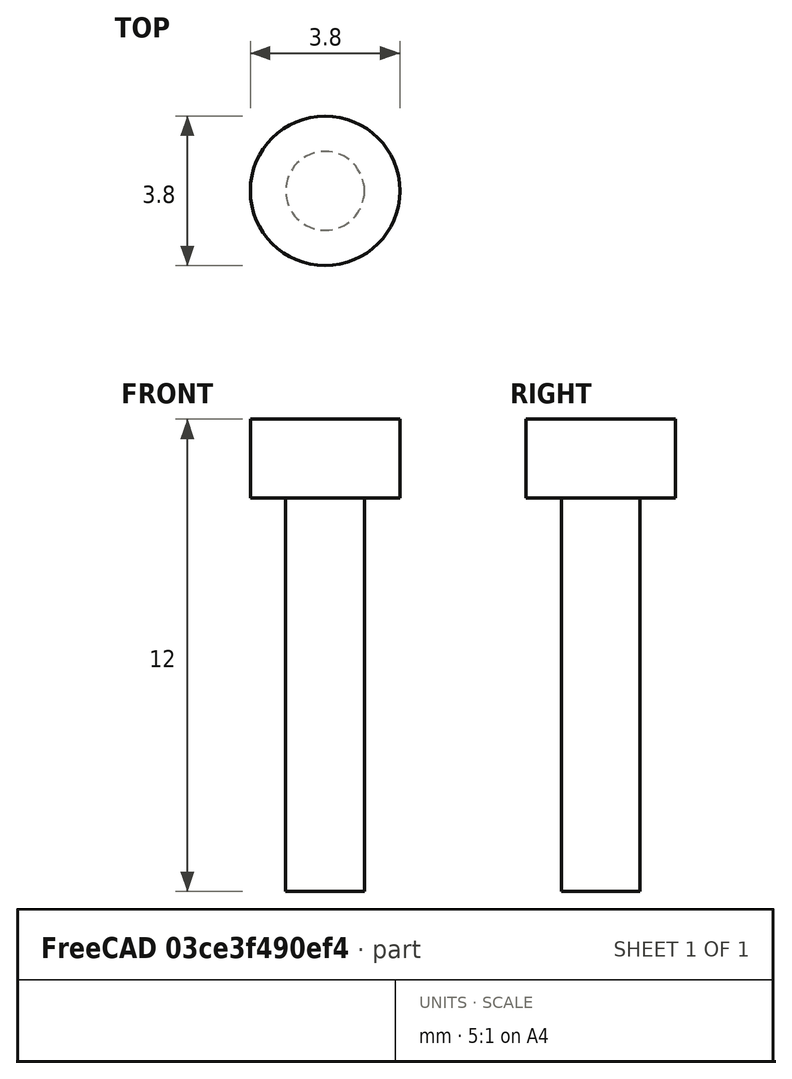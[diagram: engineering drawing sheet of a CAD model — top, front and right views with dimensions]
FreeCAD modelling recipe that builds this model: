
FCSTD DOCUMENT  (FreeCAD 0.18R14555 (Git shallow))
Label: m2-10
License: All rights reserved
LicenseURL: http://en.wikipedia.org/wiki/All_rights_reserved
objects: Sketcher::SketchObject×1, PartDesign::Revolution×1, PartDesign::Body×1
note: 4 computed .brp shape members not serialized (recipe doc carries the construction recipe); baked Part::Feature solids carry a one-line shape summary decoded from their .brp

FEATURE [Sketcher::SketchObject] Sketch
  MapMode = 5
  Placement = pos=(0,0,0) rot=(1,0,0;1.5708rad)
  Support = -> [XZ_Plane]
  sketch-geometry (6):
    g0: LineSegment StartX=0 StartY=0 StartZ=0 EndX=1 EndY=0 EndZ=0
    g1: LineSegment StartX=1 StartY=0 StartZ=0 EndX=1 EndY=10 EndZ=0
    g2: LineSegment StartX=1 StartY=10 StartZ=0 EndX=1.9 EndY=10 EndZ=0
    g3: LineSegment StartX=1.9 StartY=10 StartZ=0 EndX=1.9 EndY=12 EndZ=0
    g4: LineSegment StartX=1.9 StartY=12 StartZ=0 EndX=0 EndY=12 EndZ=0
    g5: LineSegment StartX=0 StartY=12 StartZ=0 EndX=0 EndY=0 EndZ=0
  constraints (17):
    c: Horizontal(g0)
    c: Coincident(g0,g1)
    c: Vertical(g1)
    c: Coincident(g1,g2)
    c: Horizontal(g2)
    c: Coincident(g2,g3)
    c: Coincident(g3,g4)
    c: Horizontal(g4)
    c: Coincident(g4,g5)
    c: Coincident(g5,g0)
    c: Vertical(g5)
    c: DistanceX(g0,g0) = 1
    c: DistanceY(g1,g1) = 10
    c: Vertical(g3)
    c: DistanceY(g3,g3) = 2
    c: DistanceX(g4,g4) = 1.9
    c: Coincident(g0,g-1)
FEATURE [PartDesign::Revolution] Revolution
  Angle = 360
  Axis = (0,2e-16,1)
  Base = (0,0,0)
  Placement = pos=(0,0,0) rot=(1,0,0;1.5708rad)
  Profile = -> Sketch
  ReferenceAxis = -> Sketch [V_Axis]
  Reversed = true
FEATURE [PartDesign::Body] Body
  Group = -> [Sketch,Revolution]
  Origin = -> Origin
  Tip = -> Revolution
